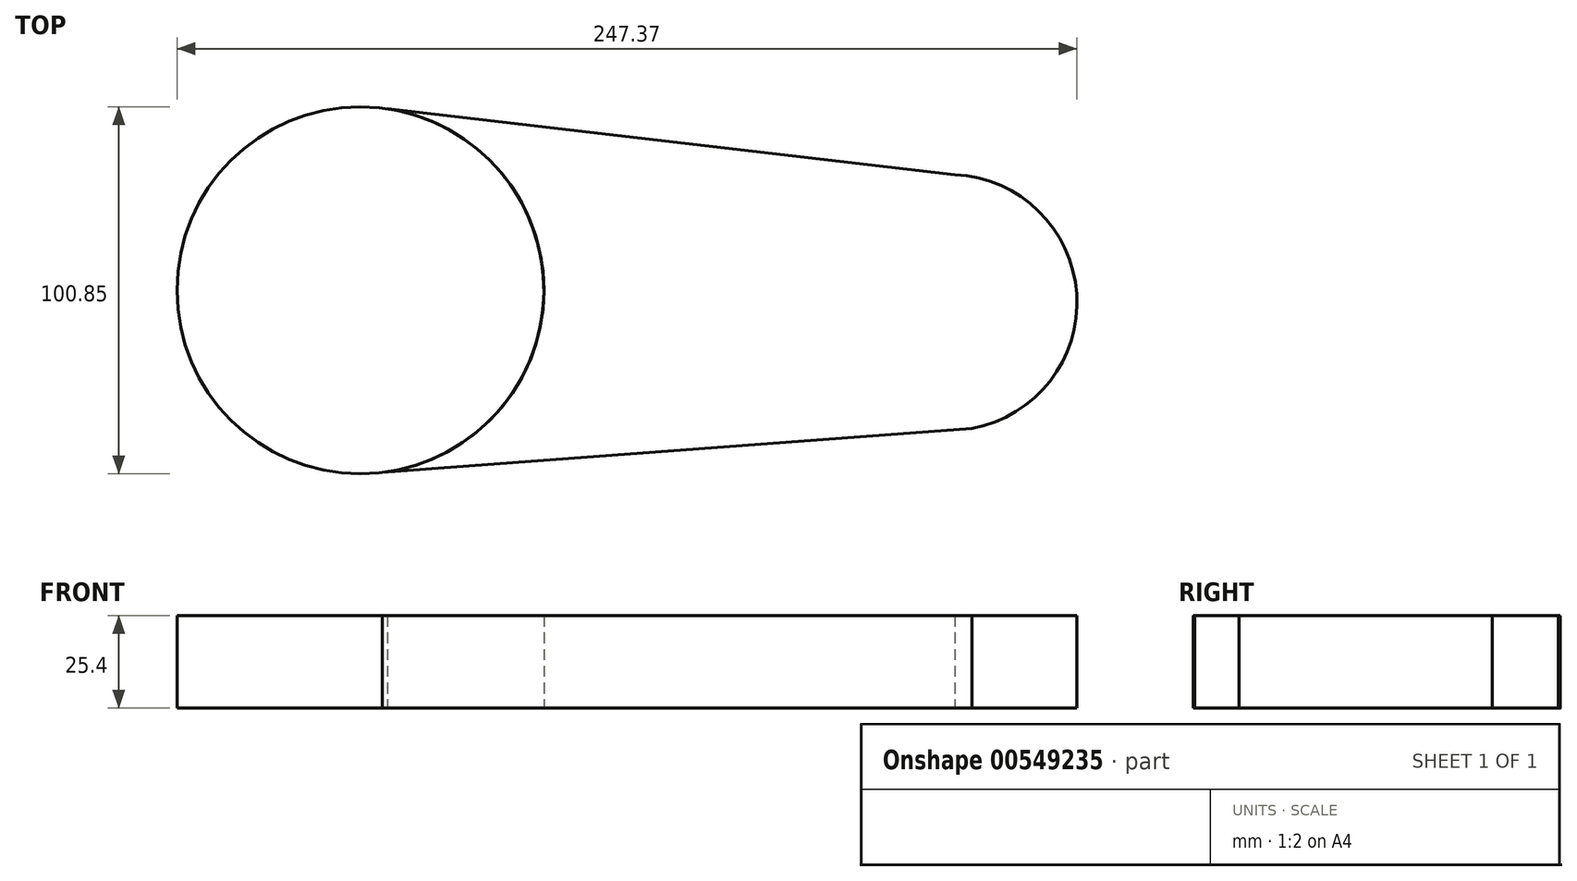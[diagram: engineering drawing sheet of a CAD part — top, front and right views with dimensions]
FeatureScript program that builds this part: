
annotation { "Feature Type Name" : "Feature", "Feature Type Description" : "" }
export const myFeature = defineFeature(function(context is Context, id is Id, definition is map)
    precondition{}
    {
        {
            var Q0;
            Q0=qCreatedBy(makeId("Top.planeOp"),FACE);
            var sketch = newSketch(context, id + "F0", { "sketchPlane" : qUnion([Q0])});
            skCircle(sketch, "E0", {"center": v(-8.3, -10.65) * mm, "radius": 50.42 * mm});
            skCircle(sketch, "E1", {"center": v(153.5, -14) * mm, "radius": 35.16 * mm});
            skLineSegment(sketch, "E2", {"start": v(-0.83, 39.22) * mm, "end": v(155.13, 21.12) * mm});
            skLineSegment(sketch, "E3", {"start": v(159.77, -48.59) * mm, "end": v(-2.22, -60.7) * mm});
            skSolve(sketch);
        }
        {
            var Q0;
            {var subQ0=sQuery(id+"F0.wireOp",EDGE,"E0");var subQ1=makeQuery(id+"F0.imprint","INTERSECT",VERTEX,{"derivedFrom":[subQ0,sQuery(id+"F0.wireOp",EDGE,"E2")]});Q0=makeQuery(id+"F0.imprint","IMPRINT",FACE,{"disambiguationData":[TD([[makeQuery(id+"F0.imprint","IMPRINT",EDGE,{"disambiguationData":[TD([[subQ1,-1.0]])],"derivedFrom":subQ0}),1.0]])]});}
            var sketch = newSketch(context, id + "F1", { "sketchPlane" : qUnion([Q0])});
            skCircle(sketch, "E4", {"center": v(151.23, 0) * mm, "radius": 12.3 * mm});
            skCircle(sketch, "E5", {"center": v(163.54, 0) * mm, "radius": 24.62 * mm});
            skSolve(sketch);
        }
        {
            var Q0;
            {var subQ0=sQuery(id+"F0.wireOp",EDGE,"E0");var subQ1=makeQuery(id+"F0.imprint","INTERSECT",VERTEX,{"derivedFrom":[subQ0,sQuery(id+"F0.wireOp",EDGE,"E2")]});Q0=makeQuery(id+"F1.imprint","IMPRINT",FACE,{"disambiguationData":[TD([[makeQuery(id+"F1.imprint","IMPRINT",EDGE,{"derivedFrom":makeQuery(id+"F0.imprint","IMPRINT",EDGE,{"disambiguationData":[TD([[subQ1,-1.0]])],"derivedFrom":subQ0})}),1.0]])]});}
            var Q1;
            {var subQ0=sQuery(id+"F0.wireOp",EDGE,"E2");Q1=makeQuery(id+"F0.imprint","IMPRINT",FACE,{"disambiguationData":[TD([[makeQuery(id+"F0.imprint","IMPRINT",EDGE,{"derivedFrom":subQ0}),-1.0]])]});}
            var Q2;
            {var subQ0=sQuery(id+"F0.wireOp",EDGE,"E1");var subQ1=makeQuery(id+"F0.imprint","INTERSECT",VERTEX,{"derivedFrom":[subQ0,sQuery(id+"F0.wireOp",EDGE,"E2")]});Q2=makeQuery(id+"F0.imprint","IMPRINT",FACE,{"disambiguationData":[TD([[makeQuery(id+"F0.imprint","IMPRINT",EDGE,{"disambiguationData":[TD([[subQ1,-1.0]])],"derivedFrom":subQ0}),1.0]])]});}
            extrude(context, id + "F2", {"entities" : qUnion([Q0, Q1, Q2]), "depth" : 25.4 * mm, "offsetDistance" : 25.4 * mm});
        }
    });
